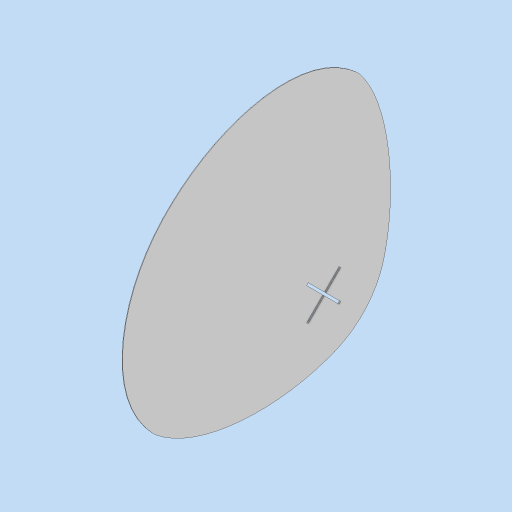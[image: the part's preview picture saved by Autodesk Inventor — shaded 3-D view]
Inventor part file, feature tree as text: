
AUTODESK INVENTOR PART (.ipt)
format: ipt  version: 2024 (Build 280153000, 153)  size: 1,233,920 bytes
history: native  units: mm
features: extrude x4, sketch x1
ambient origin geometry x8: Origin, YZ Plane, XZ Plane, XY Plane, X Axis, Y Axis, Z Axis, Center Point
bodies: Body1 (feature_tree)
feature tree (5):
  sketch  "Sketch1"  dims[d4=0.25mm d5=0.0mm d32=0.25mm d33=0.0mm d34=0.25mm d35=0.0mm d36=0.5mm d37=0.5mm d38=0.5mm d39=0.5mm d40=0.0mm d41=0.0mm d6=0.5mm d7=0.872665mm d8=0.5mm d9=0.872665mm]
  extrude  "Extrusion3"  Depth=0.25mm TaperAngle=0.0deg
  extrude  "Extrusion17"  Depth=0.25mm TaperAngle=0.0deg
  extrude  "Extrusion18"  Depth=0.5mm
  extrude  "Extrusion19"  Depth=0.5mm
